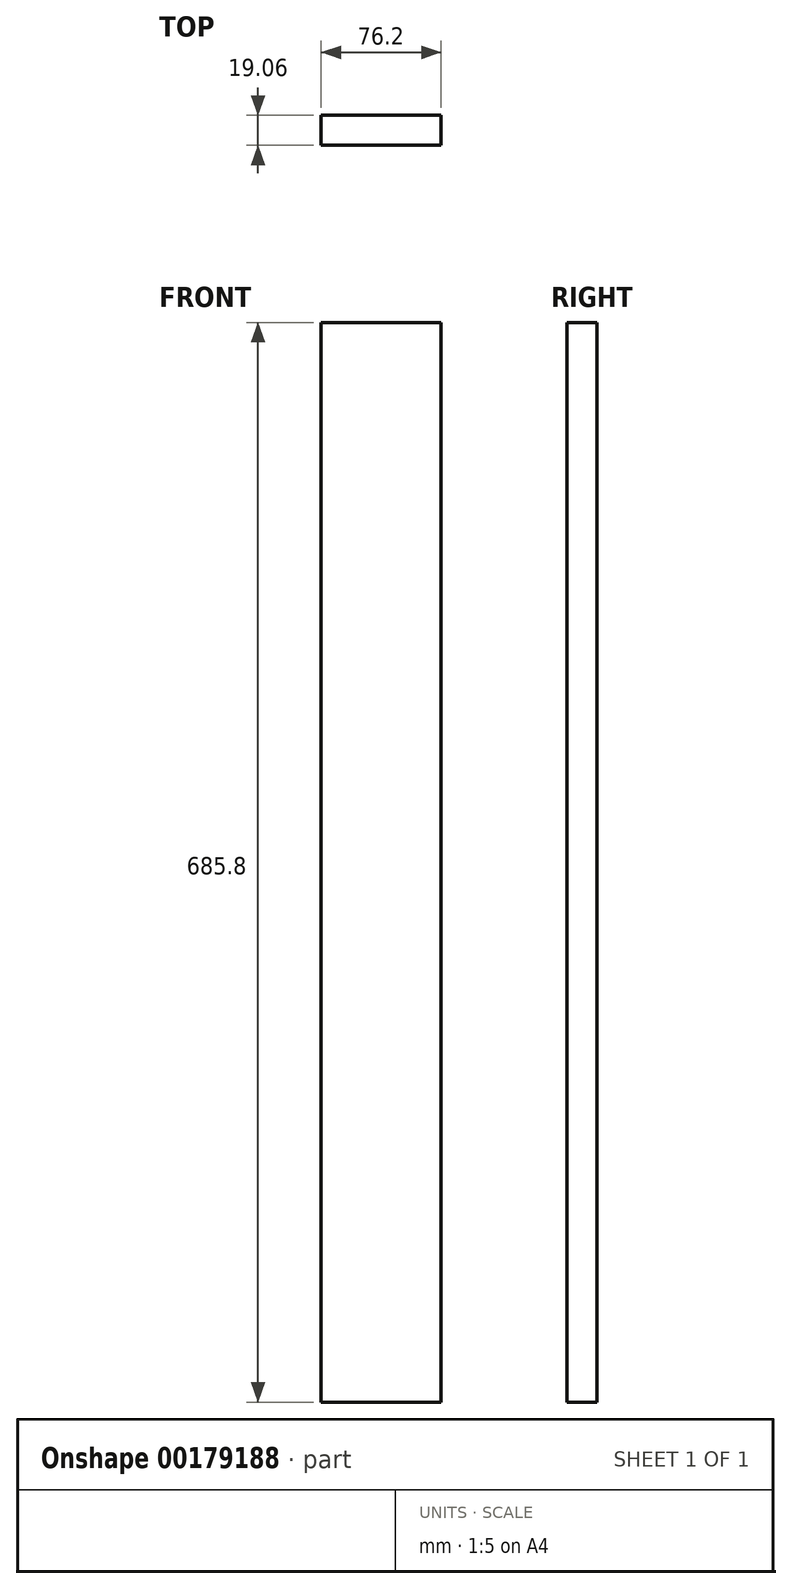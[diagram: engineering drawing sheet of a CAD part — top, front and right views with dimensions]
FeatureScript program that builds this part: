
annotation { "Feature Type Name" : "Feature", "Feature Type Description" : "" }
export const myFeature = defineFeature(function(context is Context, id is Id, definition is map)
    precondition{}
    {
        {
            var Q0;
            Q0=qCreatedBy(makeId("Front.planeOp"),FACE);
            var sketch = newSketch(context, id + "F0", { "sketchPlane" : qUnion([Q0])});
            skLineSegment(sketch, "E0.bottom", {"start": v(-70.1, 342.9) * mm, "end": v(6.1, 342.9) * mm});
            skLineSegment(sketch, "E0.top", {"start": v(-70.1, -342.9) * mm, "end": v(6.1, -342.9) * mm});
            skLineSegment(sketch, "E0.left", {"start": v(-70.1, 342.9) * mm, "end": v(-70.1, -342.9) * mm});
            skLineSegment(sketch, "E0.right", {"start": v(6.1, 342.9) * mm, "end": v(6.1, -342.9) * mm});
            skLineSegment(sketch, "E1", {"start": v(-70.1, 0) * mm, "end": v(6.1, 0) * mm});
            skSolve(sketch);
        }
        {
            var Q0;
            {var subQ0=sQuery(id+"F0.wireOp",EDGE,"E0.bottom");Q0=makeQuery(id+"F0.imprint","IMPRINT",FACE,{"disambiguationData":[TD([[makeQuery(id+"F0.imprint","IMPRINT",EDGE,{"derivedFrom":subQ0}),-1.0]])]});}
            var Q1;
            {var subQ0=sQuery(id+"F0.wireOp",EDGE,"E0.top");Q1=makeQuery(id+"F0.imprint","IMPRINT",FACE,{"disambiguationData":[TD([[makeQuery(id+"F0.imprint","IMPRINT",EDGE,{"derivedFrom":subQ0}),1.0]])]});}
            extrude(context, id + "F1", {"entities" : qUnion([Q0, Q1]), "depth" : 19.05 * mm, "symmetric" : true});
        }
    });
